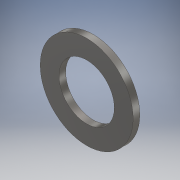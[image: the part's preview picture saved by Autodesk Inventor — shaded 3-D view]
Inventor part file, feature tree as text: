
AUTODESK INVENTOR PART (.ipt)
format: ipt  version: 2019 (Build 230136000, 136)  size: 117,248 bytes
history: native  units: mm
features: extrude x1, sketch x1
ambient origin geometry x8: Origin, YZ Plane, XZ Plane, XY Plane, X Axis, Y Axis, Z Axis, Center Point
bodies: Solid1 (feature_tree)
feature tree (2):
  extrude  "Extrusion1"  Depth=3.0mm
  sketch  "Sketch1"  dims[d0=25.0mm d1=42.0mm d2=3.0mm d3=0.0mm]
